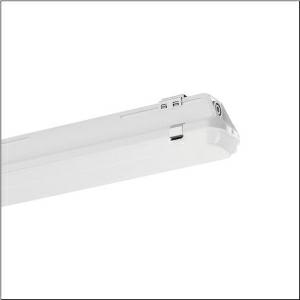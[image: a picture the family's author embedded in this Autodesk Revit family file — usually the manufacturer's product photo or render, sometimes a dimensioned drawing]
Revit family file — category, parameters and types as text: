
# Revit family: monsun_11_51fp207p430h
name_source: partatom
category: Lighting Fixtures
units: mm (PartAtom-declared; Revit-internal decimal feet)

## family parameters
Cut with Voids When Loaded = No
Host = Face
Light Source = No
Part Type = Normal
Room Calculation Point = No
Round Connector Dimension = Use Diameter
Shared = No

## types (1)
- Monsun 11 (1 x LED, 3990 lm, 24.8 W, 4000K)
    Apparent Load = 25 VA
    CIE Flux Codes = 45 75 93 94 100
    Color Rendering = 80
    Color Temperature = 4000K
    Default Elevation = 1800 mm
    Description = Monsun 11, damp-proof luminaire, chain hanger, primary optical cover: enclosure, of PC, light emission: direct distribution, primary light characteristic: symmetric, installation type: suspended mounting, surface-mounted, horizontal mounting, vertical mounting, LED, rated luminous flux: 3.990lm, luminous efficacy: 161lm/W, light colour: 840, colour temperature: 4000K, control gear: ON/OFF, with terminal, 3-pole, max. 2.5mm², mains connection: 220..240V, AC, 50/60Hz, rated input power: 25W, luminaire housing, of glass-fibre reinforced polyester, uncoated, bright grey, incl. chain hanger, length: 1.590mm, width: 90mm, height: 88mm, clip for enclosure, of stainless steel (V2A), ceiling mounting element, of stainless steel (V2A), chain hanger, of stainless steel (V2A), protection rating (complete): IP66, insulation class (complete): insulation class I (protective earthing), certification: CE, ENEC, VDE, UKCA, protection symbol: D, impact resistance: IK08, permissible operating ambient temperature: -35..+40°C, standard: EN 50419, EN 60598-2-1, no direct snow, no direct sun, no direct rain, for indoor or canopied outdoor use, corresponds to IFS (International Featured Standards) requirements for safety and quality in the food industry, contact your sales advisor before using the luminaires in applications with unclear chemical exposure, large temperature fluctuations or condensation-forming humidity, LABS conformity tested according to VDMA 24364:2018-05, packaging unit: 1 piece
    Height = 89 mm
    Lamp = 1 x LED
    Lamp Light Flux = 3990 lm
    Lamp Power = 24.8 W
    Lamp count = 1
    Length = 1590 mm
    Luminous efficacy = 161 lm/W
    Manufacturer = Siteco
    ModVariant = No
    Model = 51FP207P430H
    Mounting Place = Ceiling
    Mounting Type = Surface mounted
    Number of Poles = 1
    OnlyDefault = Yes
    Power Factor = 1
    Product Name = Monsun 11
    Product group = damp-proof luminaire
    ProductGroupID = 300
    Protection Class = Protection class I
    Protection Degree = IP 66
    RLX_Detail_Level = 1
    RLX_Emergency_Light_Flux = 0 lm
    RLX_Emergency_Type = 0
    RLX_Emergency_Type_DB = No
    RlxData = <blob elided: 88869 chars, md5=a092a55d>
    Socket = socket
    Standby Power = 0 W
    System Light Flux = 3990 lm
    System Power = 25 W
    Type Comments = Product without accessories
    Type Image = l_1349237.jpg
    URL = http://relux.com
    VarID = ---
    Voltage = 0 V
    Weight = 0.00 kg
    Width = 90 mm

## geometry (parser evidence)
native form markers: Blend x4, Sweep x14
no freeform markers — native parametric forms only
